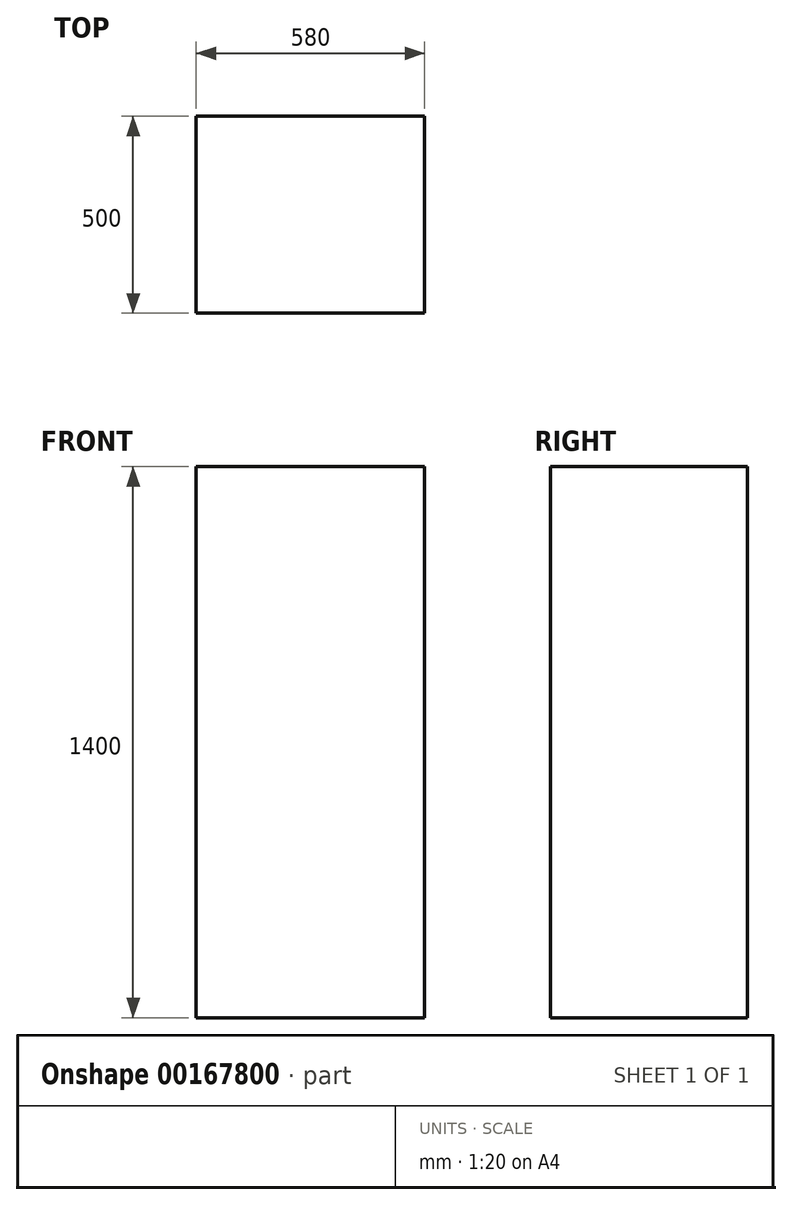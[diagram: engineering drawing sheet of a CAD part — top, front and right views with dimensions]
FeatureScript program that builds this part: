
annotation { "Feature Type Name" : "Feature", "Feature Type Description" : "" }
export const myFeature = defineFeature(function(context is Context, id is Id, definition is map)
    precondition{}
    {
        {
            var Q0;
            Q0=qCreatedBy(makeId("Top.planeOp"),FACE);
            var sketch = newSketch(context, id + "F0", { "sketchPlane" : qUnion([Q0])});
            skLineSegment(sketch, "E0.bottom", {"start": v(-290, 238.05) * mm, "end": v(290, 238.05) * mm});
            skLineSegment(sketch, "E0.top", {"start": v(-290, -261.95) * mm, "end": v(290, -261.95) * mm});
            skLineSegment(sketch, "E0.left", {"start": v(-290, 238.05) * mm, "end": v(-290, -261.95) * mm});
            skLineSegment(sketch, "E0.right", {"start": v(290, 238.05) * mm, "end": v(290, -261.95) * mm});
            skPoint(sketch, "E0.middle", {"position": v(0, -11.95) * mm});
            skSolve(sketch);
        }
        {
            var Q0;
            Q0=makeQuery(id+"F0.imprint","IMPRINT",FACE,{"disambiguationData":[TD([[makeQuery(id+"F0.imprint","IMPRINT",EDGE,{"derivedFrom":sQuery(id+"F0.wireOp",EDGE,"E0.bottom")}),-1.0]])]});
            extrude(context, id + "F1", {"entities" : qUnion([Q0]), "oppositeDirection" : true, "depth" : 1400 * mm});
        }
    });
